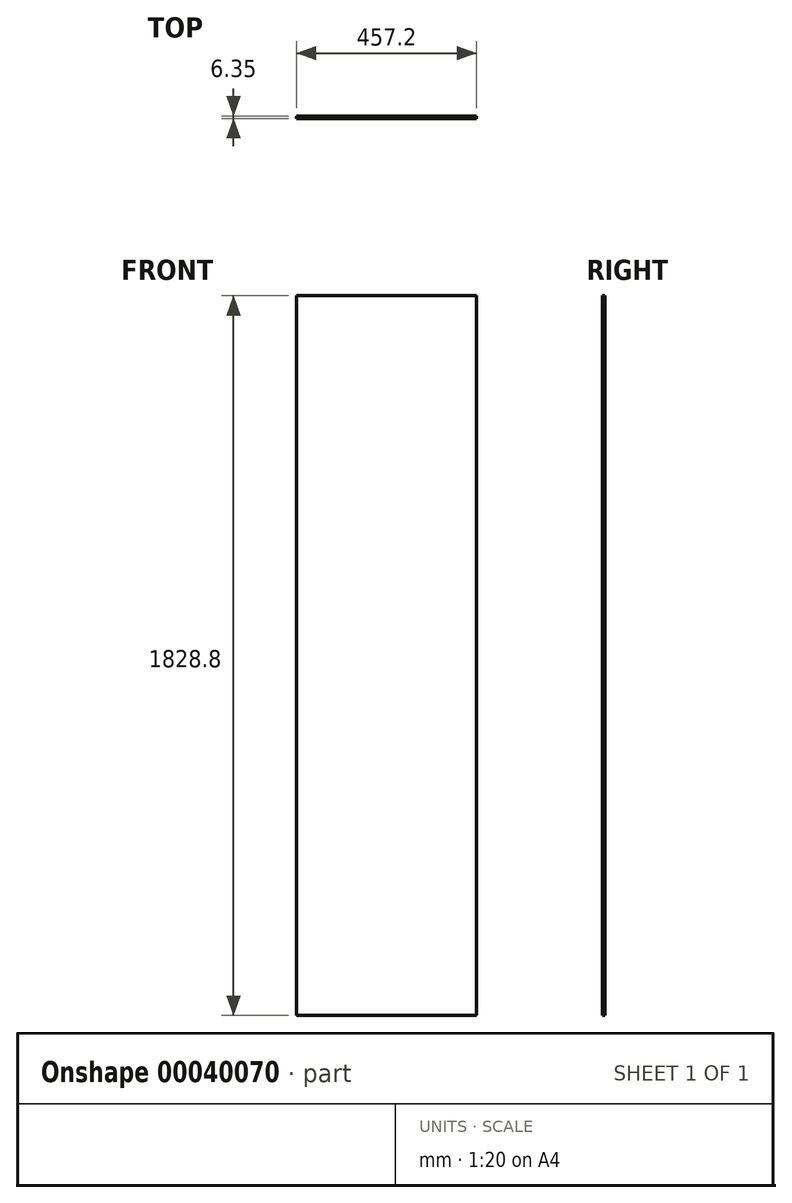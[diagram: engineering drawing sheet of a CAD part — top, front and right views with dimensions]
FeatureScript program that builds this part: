
annotation { "Feature Type Name" : "Feature", "Feature Type Description" : "" }
export const myFeature = defineFeature(function(context is Context, id is Id, definition is map)
    precondition{}
    {
        {
            var Q0;
            Q0=qCreatedBy(makeId("Front.planeOp"),FACE);
            var sketch = newSketch(context, id + "F0", { "sketchPlane" : qUnion([Q0])});
            skLineSegment(sketch, "E0.rect.bottom", {"start": v(228.6, -914.4) * mm, "end": v(-228.6, -914.4) * mm});
            skLineSegment(sketch, "E0.rect.top", {"start": v(228.6, 914.4) * mm, "end": v(-228.6, 914.4) * mm});
            skLineSegment(sketch, "E0.rect.left", {"start": v(228.6, -914.4) * mm, "end": v(228.6, 914.4) * mm});
            skLineSegment(sketch, "E0.rect.right", {"start": v(-228.6, -914.4) * mm, "end": v(-228.6, 914.4) * mm});
            skPoint(sketch, "E0.rect.middle", {"position": v(0, 0) * mm});
            skSolve(sketch);
        }
        {
            var Q0;
            Q0=qSketchRegion(id+"F0",true);
            extrude(context, id + "F1", {"entities" : qUnion([Q0]), "depth" : 6.35 * mm});
        }
    });
